# Revit family: Sink-Kitchen-KOHLER-Vault-K-3894
name_source: partatom
category: Plumbing Fixtures
revit_build: Autodesk Revit 2015 (Build: 20140606_1530(x64)
units: mm (PartAtom-declared; Revit-internal decimal feet)

## types (2) — shared parameters
ADA Compliant = Yes
Assembly Code = D2010400
CW Connection = No
Cold Water Inlet = Cold Water Inlet
Date Modified = 11/22/2017
Default Elevation = 36"
Finish = Kohler-Metal-NA-Stainless
HW Connection = No
Height = 8 3/4"
Hot Water Inlet = Hot Water Inlet
Manufacturer = KOHLER Co.
MasterFormat 1995 = 15410
MasterFormat 2004 = 22.41.16
Material = 18-gauge Stainless Steel
Product Documentation Link = http://www.us.kohler.com
Product Name = Vault
Product Page URL = http://www.us.kohler.com
URL = https://www.us.kohler.com
Vent Connection = No
Waste Connection = Yes
Waste Water Outlet = Waste Water Outlet

## per-type parameters (varying)
| type | Constraint | Description | K_3894_4 | Length | Model | Type | Width |
| Under-Mount, NA-Stainless Steel | 12" | 24inch x 18-2/7inch x 6inch under-mount single-bowl kitchen sink | No | 24" | K-3894-NA | 1 | 18 1/4" |
| Dual-Mount,4 Faucet Holes, NA-Stainless Steel | 12 1/2" | 25inch x 22inch x 6-5/16inch single bowl dual-mount kitchen sink with 4 faucet holes | Yes | 25" | K-3894-4-NA | 2 | 22" |

## geometry (parser evidence)
native form markers: Blend x2, Sweep x6
no freeform markers — native parametric forms only
